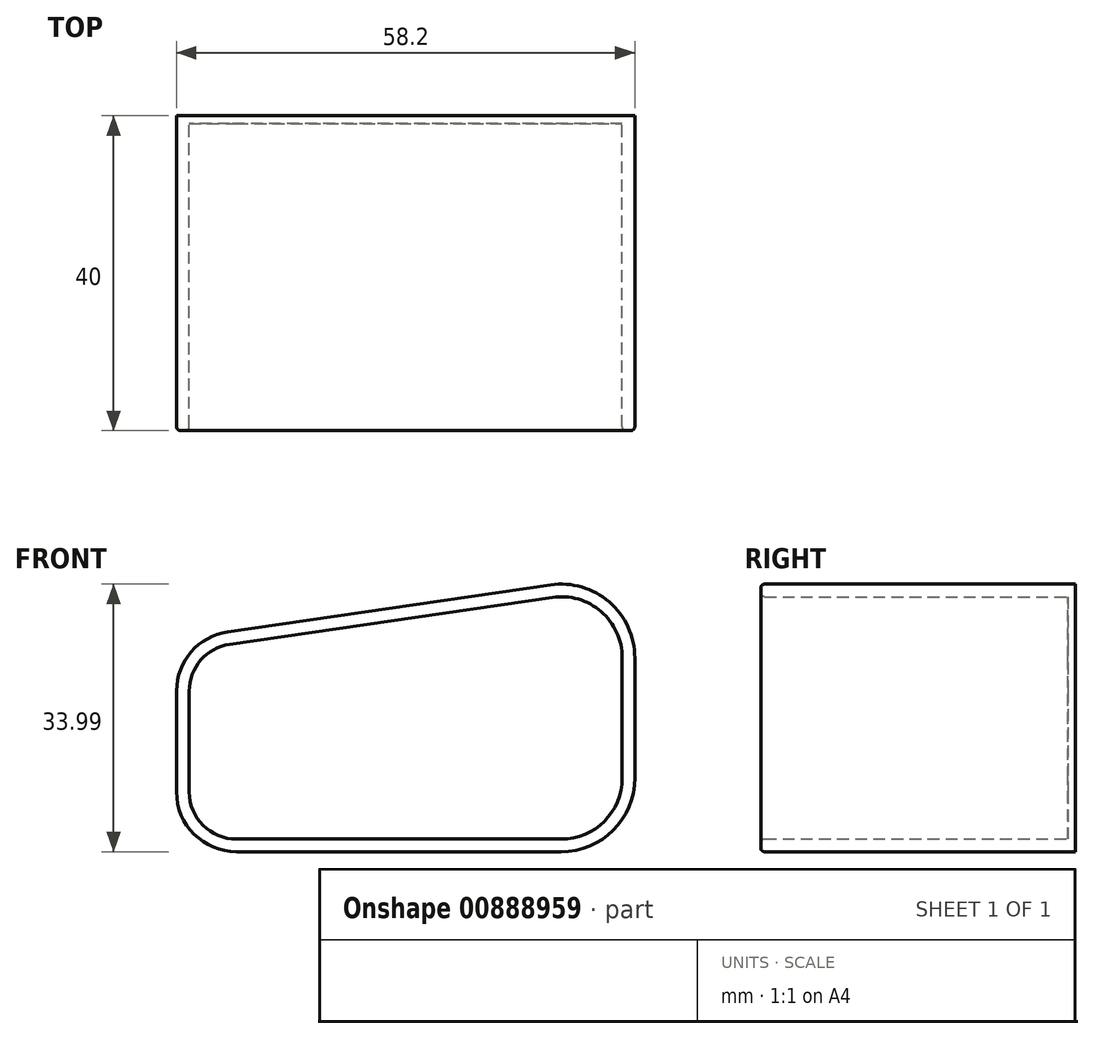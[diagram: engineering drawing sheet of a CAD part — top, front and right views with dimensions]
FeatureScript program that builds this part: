
annotation { "Feature Type Name" : "Feature", "Feature Type Description" : "" }
export const myFeature = defineFeature(function(context is Context, id is Id, definition is map)
    precondition{}
    {
        {
            var Q0;
            Q0=qCreatedBy(makeId("Front.planeOp"),FACE);
            var sketch = newSketch(context, id + "F0", { "sketchPlane" : qUnion([Q0])});
            skLineSegment(sketch, "E0", {"start": v(0, 7.75) * mm, "end": v(0, 23.04) * mm});
            skLineSegment(sketch, "E1", {"start": v(-8.87, 30.71) * mm, "end": v(-49.86, 24.75) * mm});
            skLineSegment(sketch, "E2", {"start": v(-55, 18.8) * mm, "end": v(-55, 6) * mm});
            skLineSegment(sketch, "E3", {"start": v(-49, 0) * mm, "end": v(-7.75, 0) * mm});
            skPoint(sketch, "E4.visualSharp", {"position": v(0, 32) * mm});
            skArc(sketch, "E4.filletArc", {"start": v(0, 23.04) * mm, "mid": v(-2.68, 28.9) * mm, "end": v(-8.87, 30.71) * mm});
            skPoint(sketch, "E5.visualSharp", {"position": v(0, 0) * mm});
            skArc(sketch, "E5.filletArc", {"start": v(-7.75, 0) * mm, "mid": v(-2.27, 2.27) * mm, "end": v(0, 7.75) * mm});
            skPoint(sketch, "E6.visualSharp", {"position": v(-55, 24) * mm});
            skArc(sketch, "E6.filletArc", {"start": v(-49.86, 24.75) * mm, "mid": v(-53.54, 22.74) * mm, "end": v(-55, 18.8) * mm});
            skPoint(sketch, "E7.visualSharp", {"position": v(-55, 0) * mm});
            skArc(sketch, "E7.filletArc", {"start": v(-55, 6) * mm, "mid": v(-53.24, 1.76) * mm, "end": v(-49, 0) * mm});
            skArc(sketch, "E8.0", {"start": v(-7.75, -1.6) * mm, "mid": v(-1.14, 1.14) * mm, "end": v(1.6, 7.75) * mm});
            skLineSegment(sketch, "E8.1", {"start": v(-49, -1.6) * mm, "end": v(-7.75, -1.6) * mm});
            skLineSegment(sketch, "E8.2", {"start": v(1.6, 7.75) * mm, "end": v(1.6, 23.04) * mm});
            skArc(sketch, "E8.3", {"start": v(-56.6, 6) * mm, "mid": v(-54.37, 0.63) * mm, "end": v(-49, -1.6) * mm});
            skArc(sketch, "E8.4", {"start": v(1.6, 23.04) * mm, "mid": v(-1.63, 30.11) * mm, "end": v(-9.1, 32.3) * mm});
            skLineSegment(sketch, "E8.5", {"start": v(-9.1, 32.3) * mm, "end": v(-50.1, 26.33) * mm});
            skArc(sketch, "E8.6", {"start": v(-50.1, 26.33) * mm, "mid": v(-54.75, 23.78) * mm, "end": v(-56.6, 18.8) * mm});
            skLineSegment(sketch, "E8.7", {"start": v(-56.6, 18.8) * mm, "end": v(-56.6, 6) * mm});
            skSolve(sketch);
        }
        {
            var Q0;
            Q0=makeQuery(id+"F0.imprint","IMPRINT",FACE,{"disambiguationData":[TD([[makeQuery(id+"F0.imprint","IMPRINT",EDGE,{"derivedFrom":sQuery(id+"F0.wireOp",EDGE,"E0")}),1.0]])]});
            extrude(context, id + "F1", {"entities" : qUnion([Q0]), "depth" : 1 * mm, "offsetDistance" : 25 * mm});
        }
        {
            var Q0;
            Q0 = qSketchRegion(id + "F0", true);
            extrude(context, id + "F2", {"entities" : qUnion([Q0]), "operationType" : NewBodyOperationType.ADD, "depth" : 40 * mm, "offsetDistance" : 25 * mm});
        }
        {
            var Q0;
            Q0=makeQuery(id+"F2.opExtrude","CAP_EDGE",EDGE,{"disambiguationData":[OSD([sQuery(id+"F0.wireOp",EDGE,"E8.5")])],"isStart":false});
            var Q1;
            Q1=makeQuery(id+"F2.opExtrude","CAP_EDGE",EDGE,{"disambiguationData":[OSD([sQuery(id+"F0.wireOp",EDGE,"E1")])],"isStart":false});
            fillet(context, id + "F3", {"entities" : qUnion([Q0, Q1]), "radius" : .5 * mm, "tangentPropagation" : true, "allowEdgeOverflow" : false});
        }
    });
